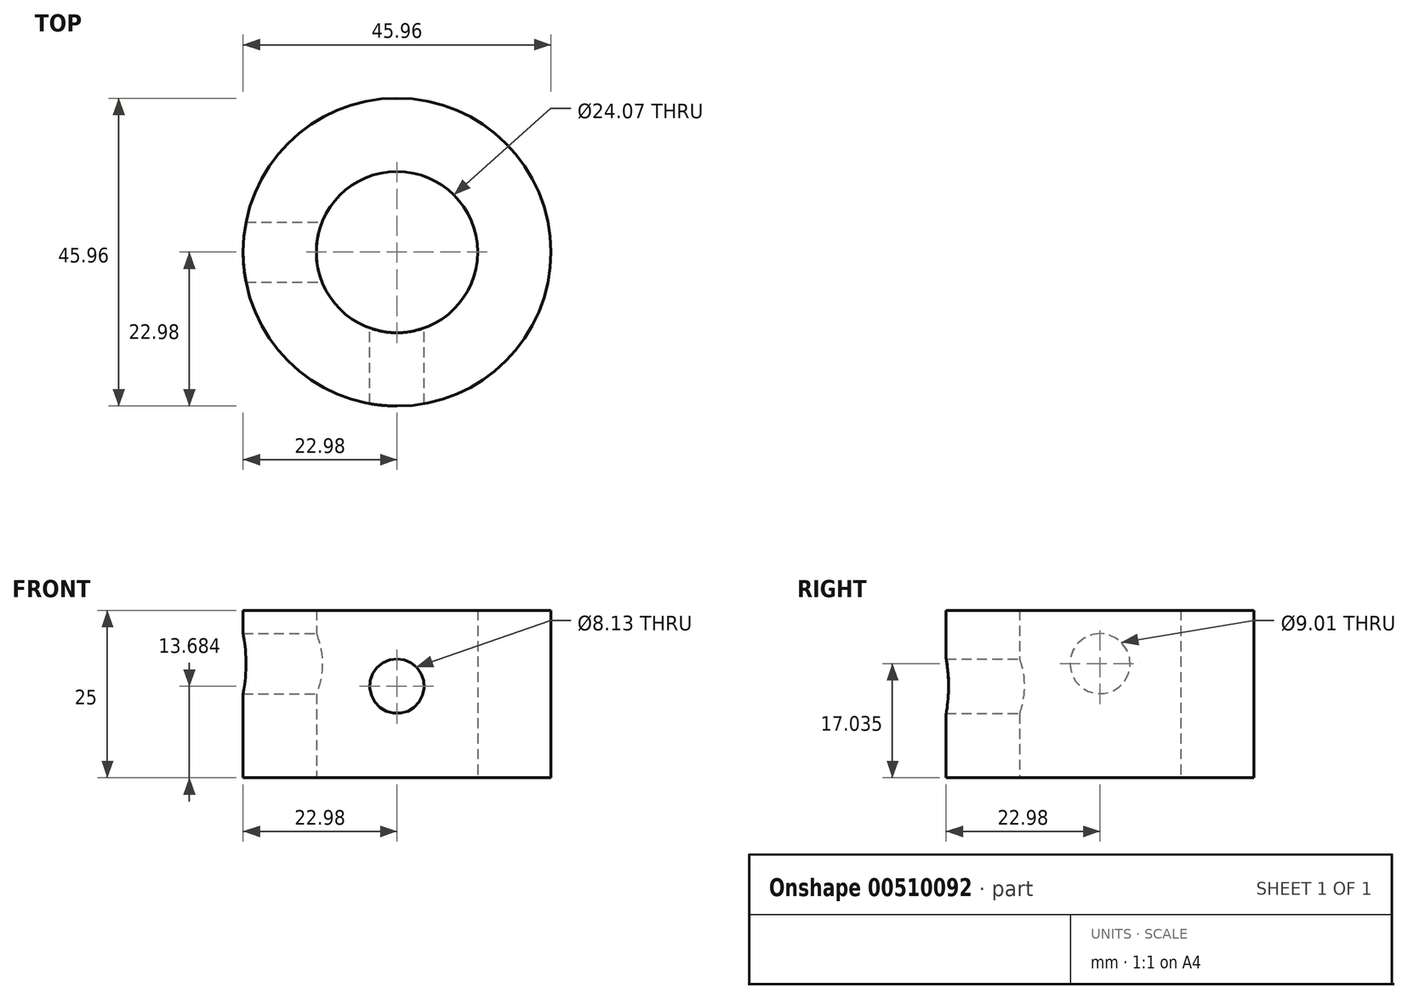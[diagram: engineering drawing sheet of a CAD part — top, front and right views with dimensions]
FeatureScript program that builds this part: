
annotation { "Feature Type Name" : "Feature", "Feature Type Description" : "" }
export const myFeature = defineFeature(function(context is Context, id is Id, definition is map)
    precondition{}
    {
        {
            var Q0;
            Q0=qCreatedBy(makeId("Top.planeOp"),FACE);
            var sketch = newSketch(context, id + "F0", { "sketchPlane" : qUnion([Q0])});
            skCircle(sketch, "E0", {"center": v(0, 0) * mm, "radius": 12.04 * mm});
            skCircle(sketch, "E1", {"center": v(0, 0) * mm, "radius": 22.98 * mm});
            skSolve(sketch);
        }
        {
            var Q0;
            Q0 = qSketchRegion(id + "F0", true);
            extrude(context, id + "F1", {"entities" : qUnion([Q0]), "depth" : 25 * mm});
        }
        {
            var Q0;
            Q0=qCreatedBy(makeId("Right.planeOp"),FACE);
            var sketch = newSketch(context, id + "F2", { "sketchPlane" : qUnion([Q0])});
            skCircle(sketch, "E2", {"center": v(0, 17.03) * mm, "radius": 4.5 * mm});
            skSolve(sketch);
        }
        {
            var Q0;
            Q0 = qSketchRegion(id + "F2", true);
            extrude(context, id + "F3", {"entities" : qUnion([Q0]), "operationType" : NewBodyOperationType.REMOVE, "endBound" : BoundingType.THROUGH_ALL, "oppositeDirection" : true, "depth" : 25 * mm});
        }
        {
            var Q0;
            Q0=qCreatedBy(makeId("Front.planeOp"),FACE);
            var sketch = newSketch(context, id + "F4", { "sketchPlane" : qUnion([Q0])});
            skCircle(sketch, "E3", {"center": v(0, 13.68) * mm, "radius": 4.07 * mm});
            skSolve(sketch);
        }
        {
            var Q0;
            Q0 = qSketchRegion(id + "F4", true);
            extrude(context, id + "F5", {"entities" : qUnion([Q0]), "operationType" : NewBodyOperationType.REMOVE, "endBound" : BoundingType.THROUGH_ALL, "depth" : 50 * mm});
        }
    });
